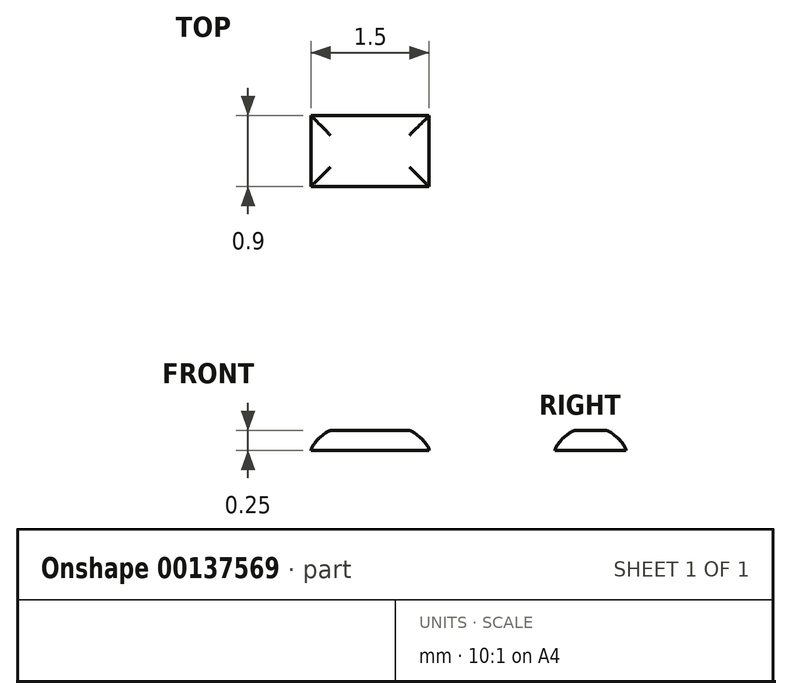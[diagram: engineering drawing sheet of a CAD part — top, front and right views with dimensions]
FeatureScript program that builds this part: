
annotation { "Feature Type Name" : "Feature", "Feature Type Description" : "" }
export const myFeature = defineFeature(function(context is Context, id is Id, definition is map)
    precondition{}
    {
        {
            var Q0;
            Q0=qCreatedBy(makeId("Top.planeOp"),FACE);
            var sketch = newSketch(context, id + "F0", { "sketchPlane" : qUnion([Q0])});
            skLineSegment(sketch, "E0.bottom", {"start": v(-0.75, 0.45) * mm, "end": v(0.75, 0.45) * mm});
            skLineSegment(sketch, "E0.top", {"start": v(-0.75, -0.45) * mm, "end": v(0.75, -0.45) * mm});
            skLineSegment(sketch, "E0.left", {"start": v(-0.75, 0.45) * mm, "end": v(-0.75, -0.45) * mm});
            skLineSegment(sketch, "E0.right", {"start": v(0.75, 0.45) * mm, "end": v(0.75, -0.45) * mm});
            skSolve(sketch);
        }
        {
            var Q0;
            Q0=makeQuery(id+"F0.imprint","IMPRINT",FACE,{"disambiguationData":[TD([[makeQuery(id+"F0.imprint","IMPRINT",EDGE,{"derivedFrom":sQuery(id+"F0.wireOp",EDGE,"E0.bottom")}),-1.0]])]});
            extrude(context, id + "F1", {"entities" : qUnion([Q0]), "depth" : .25 * mm});
        }
        {
            var Q0;
            Q0=makeQuery(id+"F1.opExtrude","CAP_EDGE",EDGE,{"disambiguationData":[OSD([sQuery(id+"F0.wireOp",EDGE,"E0.left")])],"isStart":false});
            var Q1;
            Q1=makeQuery(id+"F1.opExtrude","CAP_EDGE",EDGE,{"disambiguationData":[OSD([sQuery(id+"F0.wireOp",EDGE,"E0.top")])],"isStart":false});
            var Q2;
            Q2=makeQuery(id+"F1.opExtrude","CAP_EDGE",EDGE,{"disambiguationData":[OSD([sQuery(id+"F0.wireOp",EDGE,"E0.right")])],"isStart":false});
            var Q3;
            Q3=makeQuery(id+"F1.opExtrude","CAP_EDGE",EDGE,{"disambiguationData":[OSD([sQuery(id+"F0.wireOp",EDGE,"E0.bottom")])],"isStart":false});
            fillet(context, id + "F2", {"entities" : qUnion([Q0, Q1, Q2, Q3]), "radius" : .25 * mm, "rho" : .2, "crossSection" : FilletCrossSection.CONIC, "allowEdgeOverflow" : false});
        }
    });
